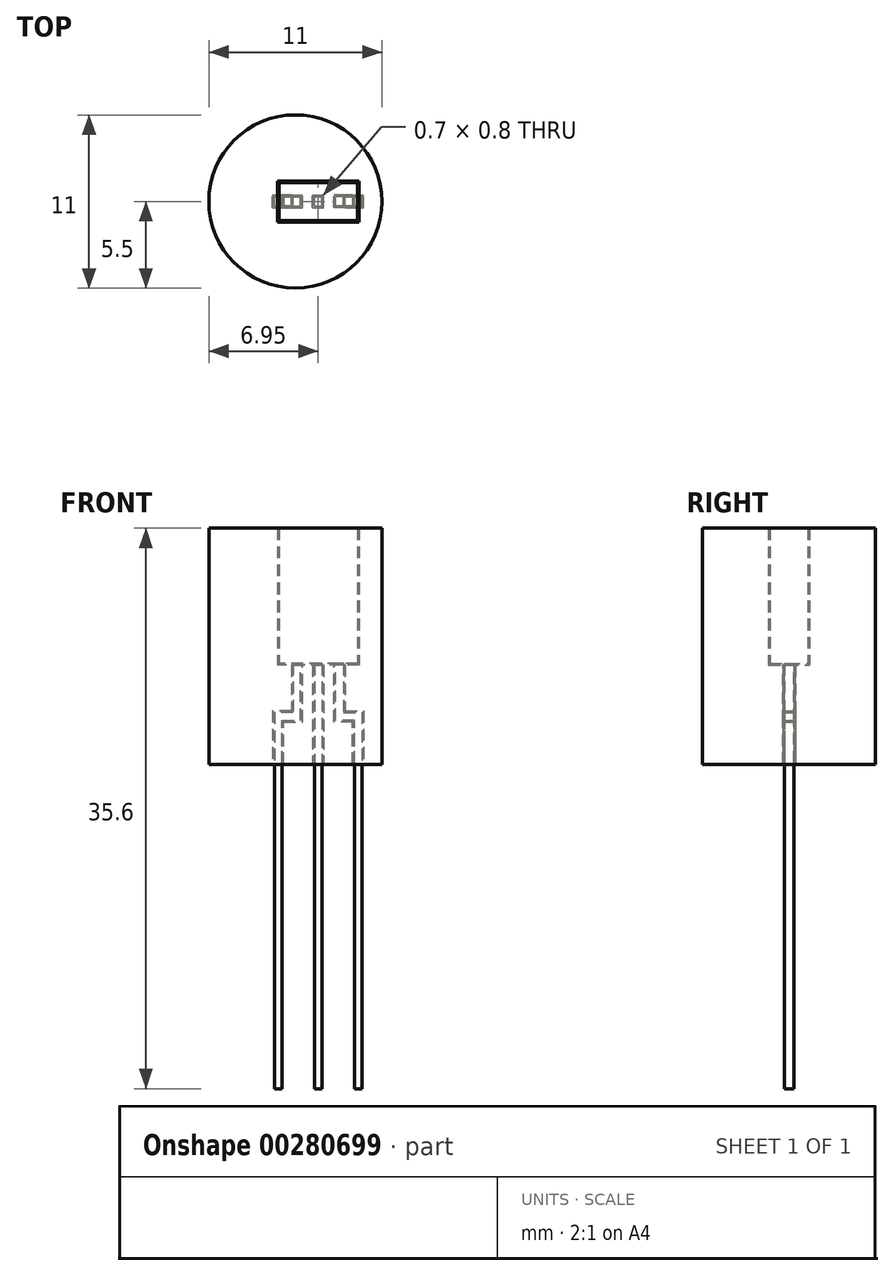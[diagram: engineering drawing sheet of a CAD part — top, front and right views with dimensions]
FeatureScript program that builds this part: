
annotation { "Feature Type Name" : "Feature", "Feature Type Description" : "" }
export const myFeature = defineFeature(function(context is Context, id is Id, definition is map)
    precondition{}
    {
        {
            assignVariable(context, id + "F0", {"name" : "laser_thickness", "anyValue" : 2.4});
        }
        {
            assignVariable(context, id + "F1", {"name" : "margin", "anyValue" : 0.1});
        }
        {
            var Q0;
            Q0=qCreatedBy(makeId("Front.planeOp"),FACE);
            var sketch = newSketch(context, id + "F2", { "sketchPlane" : qUnion([Q0])});
            skLineSegment(sketch, "E0", {"start": v(0, 8.6) * mm, "end": v(2.5, 8.6) * mm});
            skLineSegment(sketch, "E1", {"start": v(2.5, 8.6) * mm, "end": v(2.5, 0) * mm});
            skLineSegment(sketch, "E2", {"start": v(2.5, 0) * mm, "end": v(0, 0) * mm});
            skLineSegment(sketch, "E3", {"start": v(0, 10.8) * mm, "end": v(0, -8.9) * mm, "construction": true});
            skLineSegment(sketch, "E4", {"start": v(0.25, 0) * mm, "end": v(0.25, -27) * mm});
            skLineSegment(sketch, "E5", {"start": v(0.25, -27) * mm, "end": v(0, -27) * mm});
            skLineSegment(sketch, "E6", {"start": v(1.6, 0) * mm, "end": v(1.6, -3.1) * mm});
            skLineSegment(sketch, "E7", {"start": v(1.6, -3.1) * mm, "end": v(2.8, -3.1) * mm});
            skLineSegment(sketch, "E8", {"start": v(2.8, -3.1) * mm, "end": v(2.8, -27) * mm});
            skLineSegment(sketch, "E9", {"start": v(2.8, -27) * mm, "end": v(2.3, -27) * mm});
            skLineSegment(sketch, "E10", {"start": v(2.3, -27) * mm, "end": v(2.3, -3.6) * mm});
            skLineSegment(sketch, "E11", {"start": v(2.3, -3.6) * mm, "end": v(1.1, -3.6) * mm});
            skLineSegment(sketch, "E12", {"start": v(1.1, -3.6) * mm, "end": v(1.1, 0) * mm});
            skLineSegment(sketch, "E13.MirrorCS", {"start": v(-2.3, -27) * mm, "end": v(-2.3, -3.6) * mm});
            skLineSegment(sketch, "E14.MirrorCS", {"start": v(-2.8, -3.1) * mm, "end": v(-2.8, -27) * mm});
            skLineSegment(sketch, "E15.MirrorCS", {"start": v(-0.25, 0) * mm, "end": v(-0.25, -27) * mm});
            skLineSegment(sketch, "E16.MirrorCS", {"start": v(-2.8, -27) * mm, "end": v(-2.3, -27) * mm});
            skLineSegment(sketch, "E17.MirrorCS", {"start": v(-0.25, -27) * mm, "end": v(0, -27) * mm});
            skLineSegment(sketch, "E18.MirrorCS", {"start": v(-1.6, 0) * mm, "end": v(-1.6, -3.1) * mm});
            skLineSegment(sketch, "E19.MirrorCS", {"start": v(-1.1, -3.6) * mm, "end": v(-1.1, 0) * mm});
            skLineSegment(sketch, "E20.MirrorCS", {"start": v(-2.3, -3.6) * mm, "end": v(-1.1, -3.6) * mm});
            skLineSegment(sketch, "E21.MirrorCS", {"start": v(-1.6, -3.1) * mm, "end": v(-2.79, -3.1) * mm});
            skLineSegment(sketch, "E22.MirrorCS", {"start": v(-2.5, 8.6) * mm, "end": v(-2.5, 0) * mm});
            skLineSegment(sketch, "E23.MirrorCS", {"start": v(-2.5, 0) * mm, "end": v(0, 0) * mm});
            skLineSegment(sketch, "E24.MirrorCS", {"start": v(0, 8.6) * mm, "end": v(-2.5, 8.6) * mm});
            skLineSegment(sketch, "E25", {"start": v(-1.6, 0) * mm, "end": v(-1.1, 0) * mm});
            skLineSegment(sketch, "E26", {"start": v(1.1, 0) * mm, "end": v(1.6, 0) * mm});
            skLineSegment(sketch, "E27", {"start": v(-0.25, 0) * mm, "end": v(0.25, 0) * mm});
            skPoint(sketch, "E28.endSnap0", {"position": v(1.25, 8.6) * mm});
            skSolve(sketch);
        }
        {
            var Q0;
            Q0=makeQuery(id+"F2.imprint","IMPRINT",FACE,{"disambiguationData":[TD([[makeQuery(id+"F2.imprint","IMPRINT",EDGE,{"derivedFrom":sQuery(id+"F2.wireOp",EDGE,"E0")}),-1.0]])]});
            extrude(context, id + "F3", {"entities" : qUnion([Q0]), "endBound" : BoundingType.SYMMETRIC, "depth" : (getVariable(context, 'laser_thickness')) * mm});
        }
        {
            var Q0;
            Q0=makeQuery(id+"F2.imprint","IMPRINT",FACE,{"disambiguationData":[TD([[makeQuery(id+"F2.imprint","IMPRINT",EDGE,{"derivedFrom":sQuery(id+"F2.wireOp",EDGE,"E13.MirrorCS")}),1.0]])]});
            var Q1;
            Q1=makeQuery(id+"F2.imprint","IMPRINT",FACE,{"disambiguationData":[TD([[makeQuery(id+"F2.imprint","IMPRINT",EDGE,{"derivedFrom":sQuery(id+"F2.wireOp",EDGE,"E4")}),-1.0]])]});
            var Q2;
            Q2=makeQuery(id+"F2.imprint","IMPRINT",FACE,{"disambiguationData":[TD([[makeQuery(id+"F2.imprint","IMPRINT",EDGE,{"derivedFrom":sQuery(id+"F2.wireOp",EDGE,"E6")}),-1.0]])]});
            extrude(context, id + "F4", {"entities" : qUnion([Q0, Q1, Q2]), "operationType" : NewBodyOperationType.ADD, "endBound" : BoundingType.SYMMETRIC, "depth" : 0.6 * mm});
        }
        {
            var Q0;
            Q0=makeQuery(id+"F3.opExtrude","SWEPT_BODY",BODY,{"disambiguationData":[OSD([sQuery(id+"F2.wireOp",EDGE,"E0"),sQuery(id+"F2.wireOp",EDGE,"E1"),sQuery(id+"F2.wireOp",EDGE,"E2"),sQuery(id+"F2.wireOp",EDGE,"E22.MirrorCS"),sQuery(id+"F2.wireOp",EDGE,"E23.MirrorCS"),sQuery(id+"F2.wireOp",EDGE,"E24.MirrorCS"),sQuery(id+"F2.wireOp",EDGE,"E25"),sQuery(id+"F2.wireOp",EDGE,"E26"),sQuery(id+"F2.wireOp",EDGE,"E27")])]});
            transform(context, id + "F5", {"entities" : qUnion([Q0]), "transformType" : TransformType.TRANSLATION_3D, "dx" : 1.45 * mm, "dy" : 0 * mm, "dz" : 0 * mm, "makeCopy" : false});
        }
        {
            var Q0;
            Q0=qCreatedBy(makeId("Front.planeOp"),FACE);
            var sketch = newSketch(context, id + "F6", { "sketchPlane" : qUnion([Q0])});
            skLineSegment(sketch, "E29", {"start": v(0, 8.6) * mm, "end": v(5.5, 8.6) * mm});
            skLineSegment(sketch, "E30", {"start": v(5.5, 8.6) * mm, "end": v(5.5, -6.4) * mm});
            skLineSegment(sketch, "E31", {"start": v(5.5, -6.4) * mm, "end": v(0, -6.4) * mm});
            skLineSegment(sketch, "E32", {"start": v(0, -6.4) * mm, "end": v(0, 8.6) * mm});
            skLineSegment(sketch, "E33", {"start": v(-0.41, 0) * mm, "end": v(0.38, 0) * mm, "construction": true});
            skSolve(sketch);
        }
        {
            var Q0;
            Q0 = qSketchRegion(id + "F6", true);
            var Q1;
            Q1=sQuery(id+"F6.wireOp",EDGE,"E32");
            revolve(context, id + "F7", {"entities" : qUnion([Q0]), "axis" : qUnion([Q1]), "revolveType" : RevolveType.FULL});
        }
        {
            var Q0;
            Q0=makeQuery(id+"F3.opExtrude","SWEPT_BODY",BODY,{"disambiguationData":[OSD([sQuery(id+"F2.wireOp",EDGE,"E0"),sQuery(id+"F2.wireOp",EDGE,"E1"),sQuery(id+"F2.wireOp",EDGE,"E2"),sQuery(id+"F2.wireOp",EDGE,"E22.MirrorCS"),sQuery(id+"F2.wireOp",EDGE,"E23.MirrorCS"),sQuery(id+"F2.wireOp",EDGE,"E24.MirrorCS"),sQuery(id+"F2.wireOp",EDGE,"E25"),sQuery(id+"F2.wireOp",EDGE,"E26"),sQuery(id+"F2.wireOp",EDGE,"E27")])]});
            var Q1;
            Q1=makeQuery(id+"F7.opRevolve","SWEPT_BODY",BODY,{"disambiguationData":[OSD([sQuery(id+"F6.wireOp",EDGE,"E29"),sQuery(id+"F6.wireOp",EDGE,"E30"),sQuery(id+"F6.wireOp",EDGE,"E31"),sQuery(id+"F6.wireOp",EDGE,"E32")])]});
            booleanBodies(context, id + "F8", {"operationType" : BooleanOperationType.SUBTRACTION, "tools" : qUnion([Q0]), "targets" : qUnion([Q1]), "offset" : true, "offsetAll" : true, "offsetDistance" : (getVariable(context, 'margin')) * mm, "keepTools" : true});
        }
    });
